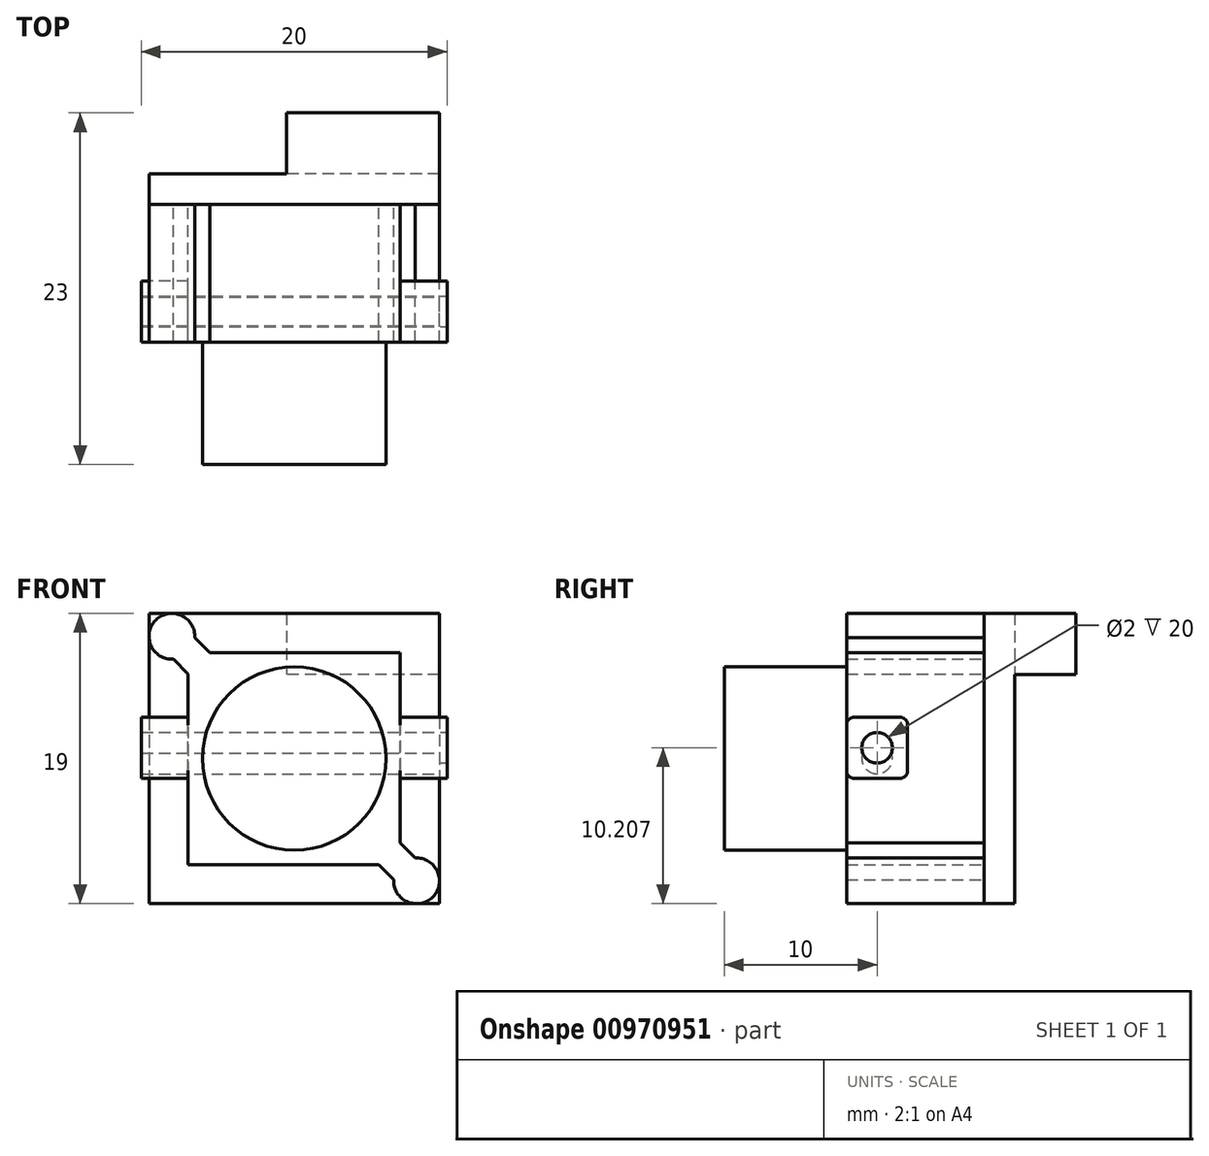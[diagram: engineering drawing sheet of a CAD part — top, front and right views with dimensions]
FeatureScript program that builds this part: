
annotation { "Feature Type Name" : "Feature", "Feature Type Description" : "" }
export const myFeature = defineFeature(function(context is Context, id is Id, definition is map)
    precondition{}
    {
        {
            var Q0;
            Q0=qCreatedBy(makeId("Front.planeOp"),FACE);
            var sketch = newSketch(context, id + "F0", { "sketchPlane" : qUnion([Q0])});
            skLineSegment(sketch, "E0.bottom", {"start": v(9.5, 9.5) * mm, "end": v(-9.5, 9.5) * mm});
            skLineSegment(sketch, "E0.top", {"start": v(9.5, -9.5) * mm, "end": v(-9.5, -9.5) * mm});
            skLineSegment(sketch, "E0.left", {"start": v(9.5, 9.5) * mm, "end": v(9.5, -9.5) * mm});
            skLineSegment(sketch, "E0.right", {"start": v(-9.5, 9.5) * mm, "end": v(-9.5, -9.5) * mm});
            skPoint(sketch, "E0.middle", {"position": v(0, 0) * mm});
            skSolve(sketch);
        }
        {
            var Q0;
            Q0=makeQuery(id+"F0.imprint","IMPRINT",FACE,{"disambiguationData":[TD([[makeQuery(id+"F0.imprint","IMPRINT",EDGE,{"derivedFrom":sQuery(id+"F0.wireOp",EDGE,"E0.bottom")}),1.0]])]});
            extrude(context, id + "F1", {"entities" : qUnion([Q0]), "depth" : 2 * mm, "offsetDistance" : 25 * mm});
        }
        {
            var Q0;
            Q0=makeQuery(id+"F1.opExtrude","CAP_FACE",FACE,{"disambiguationData":[OSD([sQuery(id+"F0.wireOp",EDGE,"E0.bottom"),sQuery(id+"F0.wireOp",EDGE,"E0.top"),sQuery(id+"F0.wireOp",EDGE,"E0.left"),sQuery(id+"F0.wireOp",EDGE,"E0.right")])],"isStart":false});
            var sketch = newSketch(context, id + "F2", { "sketchPlane" : qUnion([Q0])});
            skCircle(sketch, "E1", {"center": v(0, 0) * mm, "radius": 6 * mm});
            skSolve(sketch);
        }
        {
            var Q0;
            Q0=makeQuery(id+"F1.opExtrude","CAP_FACE",FACE,{"disambiguationData":[OSD([sQuery(id+"F0.wireOp",EDGE,"E0.bottom"),sQuery(id+"F0.wireOp",EDGE,"E0.top"),sQuery(id+"F0.wireOp",EDGE,"E0.left"),sQuery(id+"F0.wireOp",EDGE,"E0.right")])],"isStart":false});
            var sketch = newSketch(context, id + "F3", { "sketchPlane" : qUnion([Q0])});
            skArc(sketch, "E2.converted", {"start": v(-6.5, 7.92) * mm, "mid": v(-9.06, 9.06) * mm, "end": v(-7.92, 6.5) * mm});
            skArc(sketch, "E3.converted", {"start": v(6.5, -7.92) * mm, "mid": v(9.06, -9.06) * mm, "end": v(7.92, -6.5) * mm});
            skLineSegment(sketch, "E4", {"start": v(-8, 8) * mm, "end": v(8, -8) * mm, "construction": true});
            skLineSegment(sketch, "E5.bottom", {"start": v(-5.53, 6.94) * mm, "end": v(6.94, 6.94) * mm});
            skLineSegment(sketch, "E5.top", {"start": v(-6.94, -6.94) * mm, "end": v(5.53, -6.94) * mm});
            skLineSegment(sketch, "E5.left", {"start": v(-6.94, 5.53) * mm, "end": v(-6.94, -6.94) * mm});
            skLineSegment(sketch, "E5.right", {"start": v(6.94, 6.94) * mm, "end": v(6.94, -5.53) * mm});
            skLineSegment(sketch, "E6.0", {"start": v(-7.92, 6.5) * mm, "end": v(-6.94, 5.53) * mm});
            skLineSegment(sketch, "E7.0", {"start": v(-6.5, 7.92) * mm, "end": v(-5.53, 6.94) * mm});
            skLineSegment(sketch, "E8.trimOffspring", {"start": v(6.94, -5.53) * mm, "end": v(7.92, -6.5) * mm});
            skLineSegment(sketch, "E9.trimOffspring", {"start": v(5.53, -6.94) * mm, "end": v(6.5, -7.92) * mm});
            skSolve(sketch);
        }
        {
            var Q0;
            {var subQ3=sQuery(id+"F3.wireOp",EDGE,"2UgoKfpf-8lQd-A3NT-KL3H-1Nd790oDMo1S.bottom");Q0=makeQuery(id+"F3.imprint","IMPRINT",FACE,{"disambiguationData":[TD([[makeQuery(id+"F3.imprint","IMPRINT",EDGE,{"derivedFrom":subQ3}),-1.0]])]});}
            var Q1;
            Q1=makeQuery(id+"F3.imprint","IMPRINT",FACE,{"disambiguationData":[TD([[makeQuery(id+"F3.imprint","IMPRINT",EDGE,{"derivedFrom":sQuery(id+"F3.wireOp",EDGE,"E5.bottom")}),-1.0]])]});
            extrude(context, id + "F4", {"entities" : qUnion([Q0, Q1]), "depth" : 9 * mm, "offsetDistance" : 25 * mm});
        }
        {
            var Q0;
            Q0=makeQuery(id+"F2.imprint","IMPRINT",FACE,{"disambiguationData":[TD([[makeQuery(id+"F2.imprint","IMPRINT",EDGE,{"derivedFrom":sQuery(id+"F2.wireOp",EDGE,"E1")}),1.0]])]});
            var Q1;
            Q1=sQuery(id+"F2.wireOp",EDGE,"E1");
            extrude(context, id + "F5", {"entities" : qUnion([Q0]), "surfaceEntities" : qUnion([Q1]), "depth" : 17 * mm, "offsetDistance" : 25 * mm});
        }
        {
            var Q0;
            Q0=qCreatedBy(makeId("Right.planeOp"),FACE);
            var sketch = newSketch(context, id + "F6", { "sketchPlane" : qUnion([Q0])});
            skLineSegment(sketch, "E10.bottom", {"start": v(-7.5, 2.7) * mm, "end": v(-10.5, 2.7) * mm});
            skLineSegment(sketch, "E10.top", {"start": v(-7.5, -1.3) * mm, "end": v(-10.5, -1.3) * mm});
            skLineSegment(sketch, "E10.left", {"start": v(-7, 2.2) * mm, "end": v(-7, -0.8) * mm});
            skLineSegment(sketch, "E10.right", {"start": v(-11, 2.2) * mm, "end": v(-11, -0.8) * mm});
            skPoint(sketch, "E11.visualSharp", {"position": v(-11, 2.7) * mm});
            skArc(sketch, "E11.filletArc", {"start": v(-10.5, 2.7) * mm, "mid": v(-10.85, 2.56) * mm, "end": v(-11, 2.2) * mm});
            skPoint(sketch, "E12.visualSharp", {"position": v(-7, 2.7) * mm});
            skArc(sketch, "E12.filletArc", {"start": v(-7, 2.2) * mm, "mid": v(-7.15, 2.56) * mm, "end": v(-7.5, 2.7) * mm});
            skPoint(sketch, "E13.visualSharp", {"position": v(-7, -1.3) * mm});
            skArc(sketch, "E13.filletArc", {"start": v(-7.5, -1.3) * mm, "mid": v(-7.15, -1.15) * mm, "end": v(-7, -0.8) * mm});
            skPoint(sketch, "E14.visualSharp", {"position": v(-11, -1.3) * mm});
            skArc(sketch, "E14.filletArc", {"start": v(-11, -0.8) * mm, "mid": v(-10.85, -1.15) * mm, "end": v(-10.5, -1.3) * mm});
            skSolve(sketch);
        }
        {
            var Q0;
            Q0 = qSketchRegion(id + "F6", true);
            extrude(context, id + "F7", {"entities" : qUnion([Q0]), "operationType" : NewBodyOperationType.ADD, "depth" : 20 * mm, "offsetDistance" : 25 * mm, "symmetric" : true});
        }
        {
            var Q0;
            Q0=makeQuery(id+"F1.opExtrude","SWEPT_FACE",FACE,{"disambiguationData":[OSD([sQuery(id+"F0.wireOp",EDGE,"E0.left")])]});
            var sketch = newSketch(context, id + "F8", { "sketchPlane" : qUnion([Q0])});
            skCircle(sketch, "E15", {"center": v(-9, 0) * mm, "radius": 1 * mm});
            skSolve(sketch);
        }
        {
            var Q0;
            Q0=makeQuery(id+"F8.imprint","IMPRINT",FACE,{"disambiguationData":[TD([[makeQuery(id+"F8.imprint","IMPRINT",EDGE,{"derivedFrom":sQuery(id+"F8.wireOp",EDGE,"E15")}),1.0]])]});
            var Q1;
            Q1=sQuery(id+"F8.wireOp",EDGE,"E15");
            var Q2;
            Q2=makeQuery(id+"F7.opExtrude","CAP_FACE",FACE,{"disambiguationData":[OSD([sQuery(id+"F6.wireOp",EDGE,"E10.bottom"),sQuery(id+"F6.wireOp",EDGE,"E10.top"),sQuery(id+"F6.wireOp",EDGE,"E10.left"),sQuery(id+"F6.wireOp",EDGE,"E10.right"),sQuery(id+"F6.wireOp",EDGE,"E11.filletArc"),sQuery(id+"F6.wireOp",EDGE,"E12.filletArc"),sQuery(id+"F6.wireOp",EDGE,"E13.filletArc"),sQuery(id+"F6.wireOp",EDGE,"E14.filletArc")])],"isStart":true});
            extrude(context, id + "F9", {"entities" : qUnion([Q0]), "operationType" : NewBodyOperationType.REMOVE, "surfaceEntities" : qUnion([Q1]), "endBound" : BoundingType.UP_TO_SURFACE, "oppositeDirection" : true, "depth" : 25 * mm, "endBoundEntityFace" : qUnion([Q2]), "offsetDistance" : 25 * mm});
        }
        {
            var Q0;
            Q0=makeQuery(id+"F4.opExtrude","SWEPT_FACE",FACE,{"disambiguationData":[OSD([sQuery(id+"F3.wireOp",EDGE,"E5.right")])]});
            var sketch = newSketch(context, id + "F10", { "sketchPlane" : qUnion([Q0])});
            skLineSegment(sketch, "E16.0", {"start": v(-9, 6.94) * mm, "end": v(-9, -5.53) * mm, "construction": true});
            skCircle(sketch, "E17", {"center": v(-9, 0.7) * mm, "radius": 1 * mm});
            skSolve(sketch);
        }
        {
            var Q0;
            Q0=makeQuery(id+"F10.imprint","IMPRINT",FACE,{"disambiguationData":[TD([[makeQuery(id+"F10.imprint","IMPRINT",EDGE,{"derivedFrom":sQuery(id+"F10.wireOp",EDGE,"E17")}),1.0]])]});
            extrude(context, id + "F11", {"entities" : qUnion([Q0]), "operationType" : NewBodyOperationType.REMOVE, "oppositeDirection" : true, "depth" : 40 * mm, "offsetDistance" : 25 * mm, "symmetric" : true});
        }
        {
            var Q0;
            Q0=makeQuery(id+"F1.opExtrude","CAP_FACE",FACE,{"disambiguationData":[OSD([sQuery(id+"F0.wireOp",EDGE,"E0.bottom"),sQuery(id+"F0.wireOp",EDGE,"E0.top"),sQuery(id+"F0.wireOp",EDGE,"E0.left"),sQuery(id+"F0.wireOp",EDGE,"E0.right")])],"isStart":true});
            var sketch = newSketch(context, id + "F12", { "sketchPlane" : qUnion([Q0])});
            skLineSegment(sketch, "E18.bottom", {"start": v(-9.5, 9.5) * mm, "end": v(0.5, 9.5) * mm});
            skLineSegment(sketch, "E18.top", {"start": v(-9.5, 5.5) * mm, "end": v(0.5, 5.5) * mm});
            skLineSegment(sketch, "E18.left", {"start": v(-9.5, 9.5) * mm, "end": v(-9.5, 5.5) * mm});
            skLineSegment(sketch, "E18.right", {"start": v(0.5, 9.5) * mm, "end": v(0.5, 5.5) * mm});
            skSolve(sketch);
        }
        {
            var Q0;
            Q0=makeQuery(id+"F12.imprint","IMPRINT",FACE,{"disambiguationData":[TD([[makeQuery(id+"F12.imprint","IMPRINT",EDGE,{"derivedFrom":sQuery(id+"F12.wireOp",EDGE,"E18.bottom")}),-1.0]])]});
            extrude(context, id + "F13", {"entities" : qUnion([Q0]), "operationType" : NewBodyOperationType.ADD, "depth" : 4 * mm, "offsetDistance" : 25 * mm});
        }
    });
